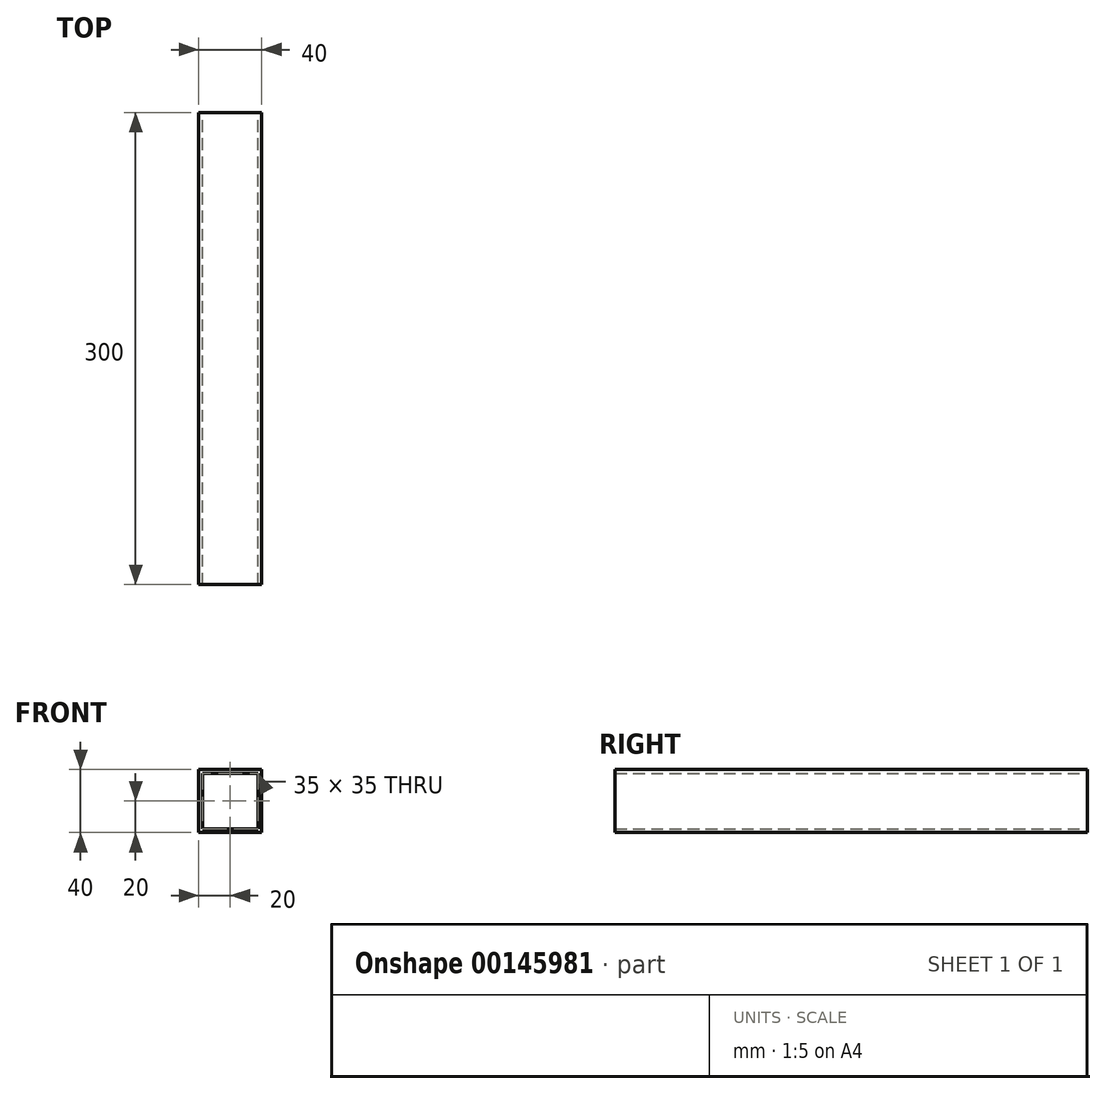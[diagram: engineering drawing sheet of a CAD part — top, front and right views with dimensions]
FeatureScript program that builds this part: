
annotation { "Feature Type Name" : "Feature", "Feature Type Description" : "" }
export const myFeature = defineFeature(function(context is Context, id is Id, definition is map)
    precondition{}
    {
        {
            var Q0;
            Q0=qCreatedBy(makeId("Front.planeOp"),FACE);
            var sketch = newSketch(context, id + "F0", { "sketchPlane" : qUnion([Q0])});
            skLineSegment(sketch, "E0.bottom", {"start": v(20, 20) * mm, "end": v(-20, 20) * mm});
            skLineSegment(sketch, "E0.top", {"start": v(20, -20) * mm, "end": v(-20, -20) * mm});
            skLineSegment(sketch, "E0.left", {"start": v(20, 20) * mm, "end": v(20, -20) * mm});
            skLineSegment(sketch, "E0.right", {"start": v(-20, 20) * mm, "end": v(-20, -20) * mm});
            skPoint(sketch, "E0.middle", {"position": v(0, 0) * mm});
            skLineSegment(sketch, "E1.bottom", {"start": v(17.5, 17.5) * mm, "end": v(-17.5, 17.5) * mm});
            skLineSegment(sketch, "E1.top", {"start": v(17.5, -17.5) * mm, "end": v(-17.5, -17.5) * mm});
            skLineSegment(sketch, "E1.left", {"start": v(17.5, 17.5) * mm, "end": v(17.5, -17.5) * mm});
            skLineSegment(sketch, "E1.right", {"start": v(-17.5, 17.5) * mm, "end": v(-17.5, -17.5) * mm});
            skSolve(sketch);
        }
        {
            var Q0;
            Q0=makeQuery(id+"F0.imprint","IMPRINT",FACE,{"disambiguationData":[TD([[makeQuery(id+"F0.imprint","IMPRINT",EDGE,{"derivedFrom":sQuery(id+"F0.wireOp",EDGE,"ZOQu13Qy-R7TU-2Z9e-bXw9-PFXj7BAkyCkY")}),1.0]])]});
            var Q1;
            Q1=makeQuery(id+"F0.imprint","IMPRINT",FACE,{"disambiguationData":[TD([[makeQuery(id+"F0.imprint","IMPRINT",EDGE,{"derivedFrom":sQuery(id+"F0.wireOp",EDGE,"E0.bottom")}),1.0]])]});
            extrude(context, id + "F1", {"entities" : qUnion([Q0, Q1]), "depth" : 300 * mm});
        }
    });
